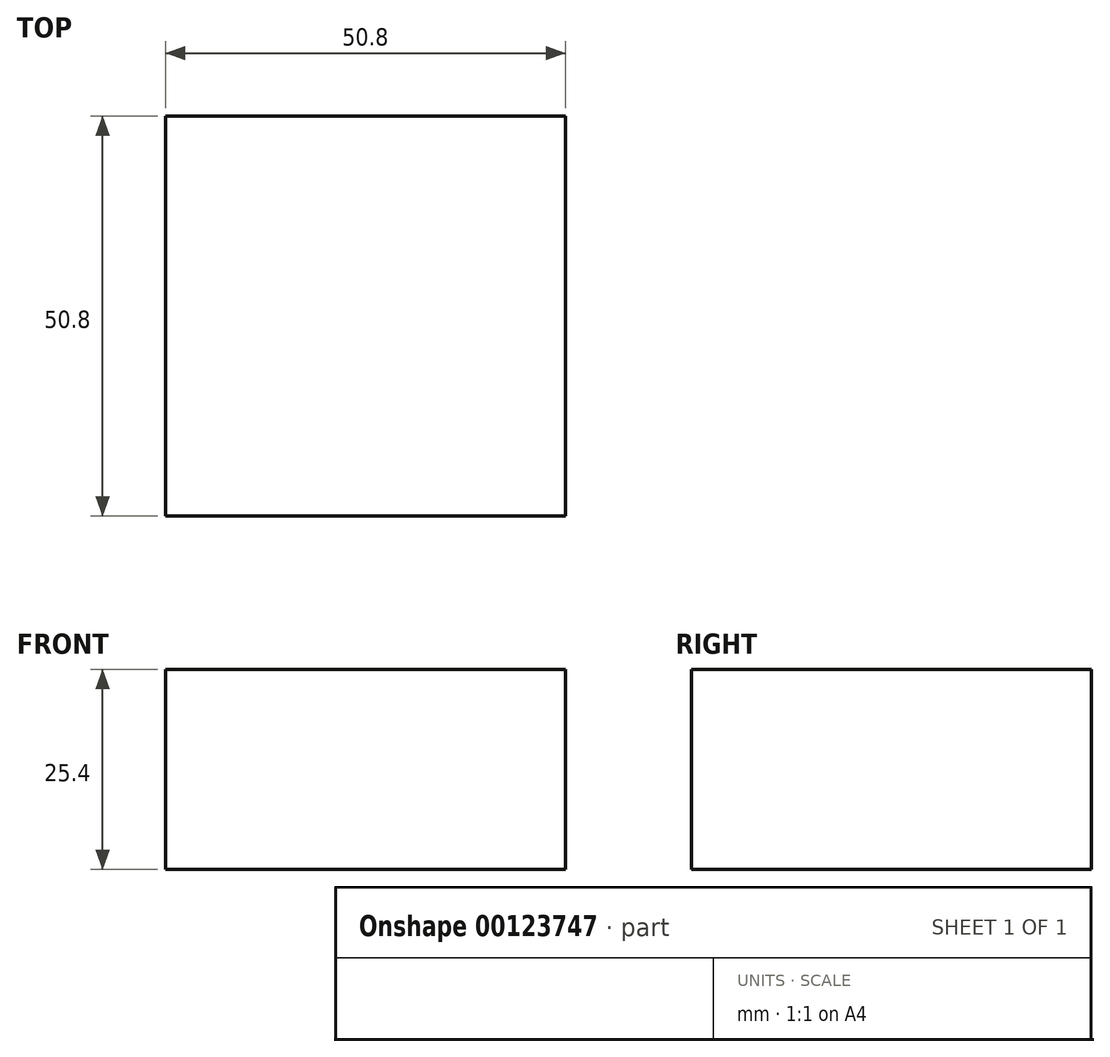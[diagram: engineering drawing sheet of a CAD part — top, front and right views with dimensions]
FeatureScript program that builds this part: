
annotation { "Feature Type Name" : "Feature", "Feature Type Description" : "" }
export const myFeature = defineFeature(function(context is Context, id is Id, definition is map)
    precondition{}
    {
        {
            var Q0;
            Q0=qCreatedBy(makeId("Top.planeOp"),FACE);
            var sketch = newSketch(context, id + "F0", { "sketchPlane" : qUnion([Q0])});
            skLineSegment(sketch, "E0.bottom", {"start": v(0, 0) * mm, "end": v(50.8, 0) * mm});
            skLineSegment(sketch, "E0.top", {"start": v(0, -50.8) * mm, "end": v(50.8, -50.8) * mm});
            skLineSegment(sketch, "E0.left", {"start": v(0, 0) * mm, "end": v(0, -50.8) * mm});
            skLineSegment(sketch, "E0.right", {"start": v(50.8, 0) * mm, "end": v(50.8, -50.8) * mm});
            skSolve(sketch);
        }
        {
            var Q0;
            Q0 = qSketchRegion(id + "F0", true);
            extrude(context, id + "F1", {"entities" : qUnion([Q0]), "depth" : 25.4 * mm});
        }
    });
